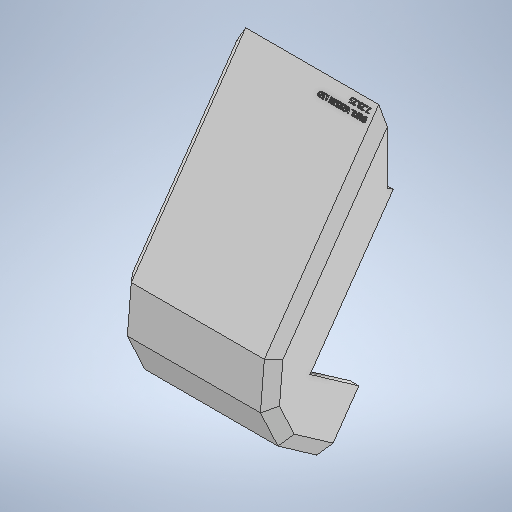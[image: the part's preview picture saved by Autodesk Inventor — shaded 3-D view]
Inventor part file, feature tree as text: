
AUTODESK INVENTOR PART (.ipt)
format: ipt  version: 2025.2 (Build 292293000, 293)  size: 1,223,168 bytes
history: native  units: in
note: dims shown in document units (in); Inventor stores cm internally (conversion verified against a paired STEP export)
features: sketch x43, extrude x39, projected_geometry x9, plane x8, move_body x1, chamfer x1, fillet x1, hole x1
ambient origin geometry x8: Origin, YZ Plane, XZ Plane, XY Plane, X Axis, Y Axis, Z Axis, Center Point
bodies: Solid1 (feature_tree)
feature tree (103):
  extrude  "Extrusion1"  Depth=0.1969in TaperAngle=0.0deg
  move_body  "Move Body1"
  plane  "Work Plane1"
  sketch  "Sketch5"  dims[d5=1.7717in d6=1.7717in d7=1.7717in d8=1.7717in d9=0.8108in d10=90.0deg d11=0.0787in d12=0.3701in d13=0.4252in d14=0.1362in d15=-0.0984in d16=-0.0591in d17=0.0in]
  plane  "Work Plane2"
  extrude  "Extrusion4"  TaperAngle=0.0deg  [1 undecoded]
  extrude  "Extrusion6"  Depth=0.2405in
  extrude  "Extrusion8"  Depth=2.5591in TaperAngle=0.0deg
  chamfer  "Chamfer1"  [1 undecoded]
  extrude  "Extrusion11"  Depth=0.2362in
  plane  "Work Plane3"
  plane  "Work Plane7"
  extrude  "Extrusion22"  Depth=0.1969in TaperAngle=0.0deg
  extrude  "Extrusion25"  Depth=0.5027in
  extrude  "Extrusion26"  Depth=0.5027in
  sketch  "Sketch33"  dims[d96=0.2362in d97=0.0in d100=3.6403in]
  extrude  "Extrusion27"  Depth=0.2362in TaperAngle=0.0deg
  extrude  "Extrusion28"  Depth=0.2362in
  sketch  "Sketch36"  dims[d123=0.9331in d124=0.9712in d125=0.0in]
  extrude  "Extrusion29"  Depth=1.9685in
  extrude  "Extrusion30"  Depth=0.1575in
  extrude  "Extrusion31"  Depth=0.9712in TaperAngle=0.0deg
  sketch  "Sketch39"  dims[d138=0.4331in d139=0.1181in d140=0.0in]
  extrude  "Extrusion32"  Depth=11.3469in TaperAngle=0.0deg
  fillet  "Fillet1"  Radius=11.3469in
  extrude  "Extrusion33"  Depth=0.4331in
  extrude  "Extrusion34"  Depth=0.1181in TaperAngle=0.0deg
  extrude  "Extrusion35"  Depth=0.0787in
  plane  "Work Plane8"
  sketch  "Sketch45"  dims[d160=0.1181in d161=0.0in d162=0.1969in d163=0.0in d164=0.1181in d165=0.0in]
  extrude  "Extrusion37"  Depth=0.2756in
  extrude  "Extrusion38"  Depth=0.1181in TaperAngle=0.0deg
  extrude  "Extrusion40"  Depth=0.5906in
  extrude  "Extrusion41"  Depth=0.1969in TaperAngle=0.0deg
  extrude  "Extrusion43"  Depth=4.7244in TaperAngle=0.0deg
  extrude  "Extrusion44"  Depth=0.7313in TaperAngle=0.0deg
  extrude  "Extrusion46"  TaperAngle=0.0deg  [1 undecoded]
  extrude  "Extrusion48"  Depth=1.1024in
  extrude  "Extrusion50"  Depth=0.0394in TaperAngle=0.0deg
  extrude  "Extrusion51"  Depth=5.8937in TaperAngle=0.0deg
  extrude  "Extrusion53"  Depth=0.5917in TaperAngle=0.0deg
  plane  "Work Plane9"
  extrude  "Extrusion55"  TaperAngle=0.0deg  [1 undecoded]
  extrude  "Extrusion56"  Depth=1.1811in TaperAngle=0.0deg
  plane  "Work Plane10"
  extrude  "Extrusion57"  TaperAngle=0.0deg  [1 undecoded]
  plane  "Work Plane11"
  extrude  "Extrusion58"  TaperAngle=0.0deg  [1 undecoded]
  extrude  "Extrusion59"  Depth=0.2362in TaperAngle=0.0deg
  extrude  "Extrusion60"  Depth=0.2362in TaperAngle=0.0deg
  extrude  "Extrusion61"  Depth=0.0394in TaperAngle=0.0deg
  extrude  "Extrusion62"  Depth=0.1969in
  extrude  "Extrusion63"  TaperAngle=60.0deg  [1 undecoded]
  extrude  "Extrusion64"  Depth=3.9671in
  extrude  "Extrusion65"  Depth=0.0197in
  sketch  "Sketch1"  dims[d1=0.5512in d2=0.1969in d3=0.0in]
  sketch  "Sketch6"  dims[d18=0.2749in d24=0.2405in]
  sketch  "Sketch8"  dims[d25=2.7559in d26=0.0in d29=2.5591in d30=0.0in d36=0.0in d37=0.0in]
  sketch  "Sketch12"  dims[d42=0.2362in d43=0.2362in]
  sketch  "Sketch15"  dims[d52=0.2362in d53=0.0787in d54=45.0deg d55=0.1969in d56=0.0in]
  sketch  "Sketch28"  dims[d76=0.5027in d77=0.5027in]
  sketch  "Sketch31"  dims[d78=0.5027in d79=0.5027in]
  sketch  "Sketch32"  dims[d83=0.0in d84=0.0in d94=0.2362in d95=0.0in]
  sketch  "Sketch34"  dims[d101=2.7717in d112=1.9685in]
  sketch  "Sketch35"  dims[d113=0.6299in d114=0.0in d115=0.1575in d117=0.1575in d121=1.9685in d122=0.7874in]
  sketch  "Sketch37"  dims[d126=0.5906in d127=0.0in d128=11.3469in d129=0.0in d130=11.3469in d131=0.0in]
  sketch  "Sketch38"  dims[d136=0.4331in d137=0.4331in]
  sketch  "Sketch40"  dims[d141=0.6299in d142=0.0787in]
  sketch  "Sketch41"  dims[d147=0.2756in d149=0.2756in]
  sketch  "Sketch42"  dims[d150=0.0in d151=0.0in d154=0.1181in d155=0.0in]
  sketch  "Sketch44"  dims[d156=0.1181in d157=0.0in d158=0.5906in]
  projected_geometry  "Projected Loop2"
  projected_geometry  "Projected Loop3"
  projected_geometry  "Projected Loop5"
  sketch  "Sketch47"  dims[d168=0.5906in d169=0.0in d170=4.7244in d171=0.0in]
  sketch  "Sketch49"  dims[d174=0.0in d175=0.0in d176=0.7313in d177=0.0in]
  sketch  "Sketch50"  dims[d186=0.0in d187=0.0in d188=0.0in d189=0.0in]
  sketch  "Sketch52"  dims[d194=0.0in d195=0.0in d196=1.1024in]
  sketch  "Sketch53"  dims[d197=0.5906in d200=0.0394in d201=0.0in]
  sketch  "Sketch56"  dims[d218=0.0in d219=0.0in d220=5.8937in d221=0.0in]
  sketch  "Sketch59"  dims[d233=0.9963in d234=0.5917in d235=0.0in]
  sketch  "Sketch60"  dims[d241=1.378in d242=0.0in d243=0.0in d244=0.0in]
  sketch  "Sketch61"  dims[d245=120.0deg d246=1.1811in d247=0.0in]
  sketch  "Sketch63"  dims[d248=120.0deg d249=0.0in d250=0.0in]
  projected_geometry  "Projected Loop8"
  sketch  "Sketch65"  dims[d251=0.7874in d252=0.0in d253=0.0in d254=0.0in]
  projected_geometry  "Projected Loop9"
  sketch  "Sketch67"  dims[d255=0.2362in d256=0.0in d257=0.2362in d258=0.0in]
  sketch  "Sketch68"  dims[d259=0.2362in d260=0.5118in d261=0.0in]
  projected_geometry  "Projected Loop10"
  sketch  "Sketch69"  dims[d262=0.1082in d263=0.0394in d264=0.0in]
  sketch  "Sketch70"  dims[d266=0.1378in d268=0.1969in]
  projected_geometry  "Projected Loop11"
  sketch  "Sketch71"  dims[d269=0.1378in d270=60.0deg]
  projected_geometry  "Projected Loop12"
  sketch  "Sketch72"  dims[d271=3.9671in d272=0.0in d38=0.0197in]
  sketch  "Sketch73"  dims[d39=0.0344in d57=0.0197in]
  sketch  "Sketch74"  dims[d58=0.0344in d59=0.0197in]
  projected_geometry  "Projected Loop13"
  sketch  "Sketch75"  dims[d60=0.0344in]
  sketch  "Sketch76"  dims[d81=0.0197in d82=0.0344in d159=0.0344in d178=0.0in d179=0.0in d180=0.0in d181=0.0in d202=0.0197in d203=0.0344in d222=0.0197in d223=0.0344in]
  sketch  "Sketch2"  dims[d4=0.315in]
  hole  "Hole1"  [1 undecoded]
note: 8 required parameter values undecoded (feature->parameter linkage not recoverable at this tier; creation-order binding heuristic only, values carry confidence <= 0.55)
